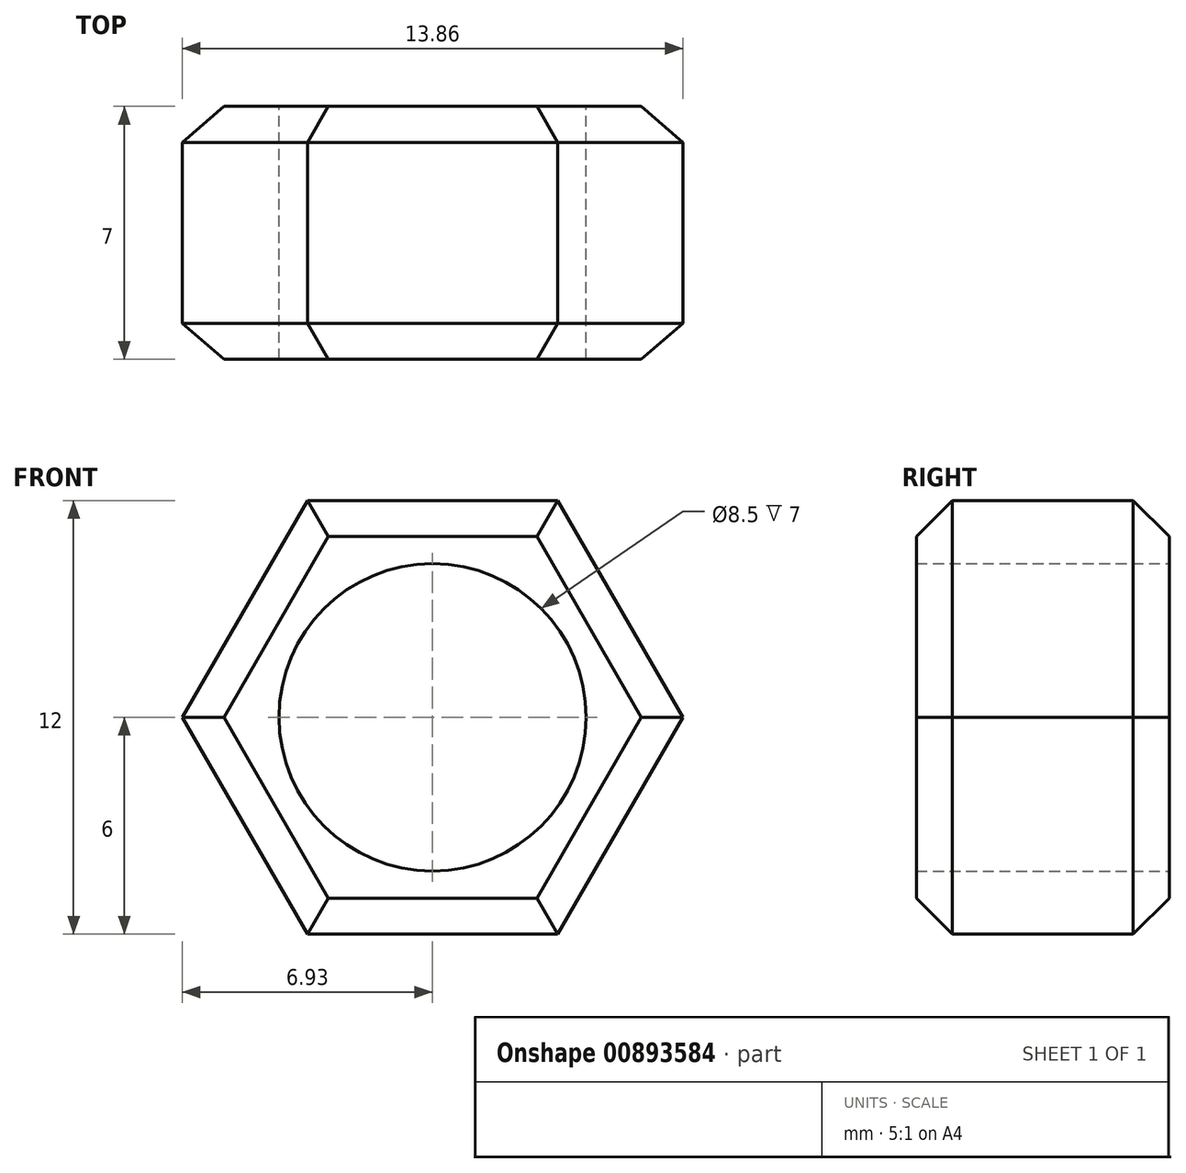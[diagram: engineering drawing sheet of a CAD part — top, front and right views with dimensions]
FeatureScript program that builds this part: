
annotation { "Feature Type Name" : "Feature", "Feature Type Description" : "" }
export const myFeature = defineFeature(function(context is Context, id is Id, definition is map)
    precondition{}
    {
        {
            var Q0;
            Q0=qCreatedBy(makeId("Front.planeOp"),FACE);
            var sketch = newSketch(context, id + "F0", { "sketchPlane" : qUnion([Q0])});
            skCircle(sketch, "E0.cCircle", {"center": v(0, 0) * mm, "radius": 6 * mm, "construction": true});
            skLineSegment(sketch, "E0.0", {"start": v(-3.46, 6) * mm, "end": v(3.46, 6) * mm});
            skLineSegment(sketch, "E0.1", {"start": v(3.46, 6) * mm, "end": v(6.93, 0) * mm});
            skLineSegment(sketch, "E0.2", {"start": v(6.93, 0) * mm, "end": v(3.46, -6) * mm});
            skLineSegment(sketch, "E0.3", {"start": v(3.46, -6) * mm, "end": v(-3.46, -6) * mm});
            skLineSegment(sketch, "E0.4", {"start": v(-3.46, -6) * mm, "end": v(-6.93, 0) * mm});
            skLineSegment(sketch, "E0.5", {"start": v(-6.93, 0) * mm, "end": v(-3.46, 6) * mm});
            skPoint(sketch, "E0.0.midPoint", {"position": v(0, 6) * mm});
            skSolve(sketch);
        }
        {
            var Q0;
            Q0=makeQuery(id+"F0.imprint","IMPRINT",FACE,{"disambiguationData":[TD([[makeQuery(id+"F0.imprint","IMPRINT",EDGE,{"derivedFrom":sQuery(id+"F0.wireOp",EDGE,"E0.0")}),-1.0]])]});
            extrude(context, id + "F1", {"entities" : qUnion([Q0]), "depth" : 7 * mm, "offsetDistance" : 25 * mm});
        }
        {
            var Q0;
            Q0=sQuery(id+"F0.wireOp",VERTEX,"E0.cCircle.center");
            var Q1;
            Q1=makeQuery(id+"F1.opExtrude","SWEPT_BODY",BODY,{"disambiguationData":[OSD([sQuery(id+"F0.wireOp",EDGE,"E0.0"),sQuery(id+"F0.wireOp",EDGE,"E0.1"),sQuery(id+"F0.wireOp",EDGE,"E0.2"),sQuery(id+"F0.wireOp",EDGE,"E0.3"),sQuery(id+"F0.wireOp",EDGE,"E0.4"),sQuery(id+"F0.wireOp",EDGE,"E0.5")])]});
            hole(context, id + "F2", {"style" : HoleStyle.SIMPLE, "endStyle" : HoleEndStyle.THROUGH, "oppositeDirection" : true, "standardTappedOrClearance" : lookupTablePath({ "standard" : "ISO", "engagement" : "75%", "pitch" : "1.5 mm", "size" : "M10", "type" : "Tapped" }), "standardBlindInLast" : lookupTablePath({ "standard" : "ISO", "engagement" : "75%", "pitch" : "1.5 mm", "size" : "M10", "type" : "Tapped" }), "holeDiameter" : 8.5 * mm, "majorDiameter" : 10 * mm, "showTappedDepth" : true, "isTappedThrough" : true, "tappedDepth" : 12 * mm, "tapClearance" : 3, "locations" : qUnion([Q0]), "scope" : qUnion([Q1])});
        }
        {
            var Q0;
            Q0=makeQuery(id+"F1.opExtrude","CAP_EDGE",EDGE,{"disambiguationData":[OSD([sQuery(id+"F0.wireOp",EDGE,"E0.0")])],"isStart":false});
            var Q1;
            Q1=makeQuery(id+"F1.opExtrude","CAP_EDGE",EDGE,{"disambiguationData":[OSD([sQuery(id+"F0.wireOp",EDGE,"E0.5")])],"isStart":false});
            var Q2;
            Q2=makeQuery(id+"F1.opExtrude","CAP_EDGE",EDGE,{"disambiguationData":[OSD([sQuery(id+"F0.wireOp",EDGE,"E0.4")])],"isStart":false});
            var Q3;
            Q3=makeQuery(id+"F1.opExtrude","CAP_EDGE",EDGE,{"disambiguationData":[OSD([sQuery(id+"F0.wireOp",EDGE,"E0.3")])],"isStart":false});
            var Q4;
            Q4=makeQuery(id+"F1.opExtrude","CAP_EDGE",EDGE,{"disambiguationData":[OSD([sQuery(id+"F0.wireOp",EDGE,"E0.2")])],"isStart":false});
            var Q5;
            Q5=makeQuery(id+"F1.opExtrude","CAP_EDGE",EDGE,{"disambiguationData":[OSD([sQuery(id+"F0.wireOp",EDGE,"E0.1")])],"isStart":false});
            var Q6;
            Q6=makeQuery(id+"F1.opExtrude","CAP_EDGE",EDGE,{"disambiguationData":[OSD([sQuery(id+"F0.wireOp",EDGE,"E0.1")])],"isStart":true});
            var Q7;
            Q7=makeQuery(id+"F1.opExtrude","CAP_EDGE",EDGE,{"disambiguationData":[OSD([sQuery(id+"F0.wireOp",EDGE,"E0.0")])],"isStart":true});
            var Q8;
            Q8=makeQuery(id+"F1.opExtrude","CAP_EDGE",EDGE,{"disambiguationData":[OSD([sQuery(id+"F0.wireOp",EDGE,"E0.5")])],"isStart":true});
            var Q9;
            Q9=makeQuery(id+"F1.opExtrude","CAP_EDGE",EDGE,{"disambiguationData":[OSD([sQuery(id+"F0.wireOp",EDGE,"E0.4")])],"isStart":true});
            var Q10;
            Q10=makeQuery(id+"F1.opExtrude","CAP_EDGE",EDGE,{"disambiguationData":[OSD([sQuery(id+"F0.wireOp",EDGE,"E0.3")])],"isStart":true});
            var Q11;
            Q11=makeQuery(id+"F1.opExtrude","CAP_EDGE",EDGE,{"disambiguationData":[OSD([sQuery(id+"F0.wireOp",EDGE,"E0.2")])],"isStart":true});
            chamfer(context, id + "F3", {"entities" : qUnion([Q0, Q1, Q2, Q3, Q4, Q5, Q6, Q7, Q8, Q9, Q10, Q11]), "width" : 1 * mm, "tangentPropagation" : true});
        }
    });
